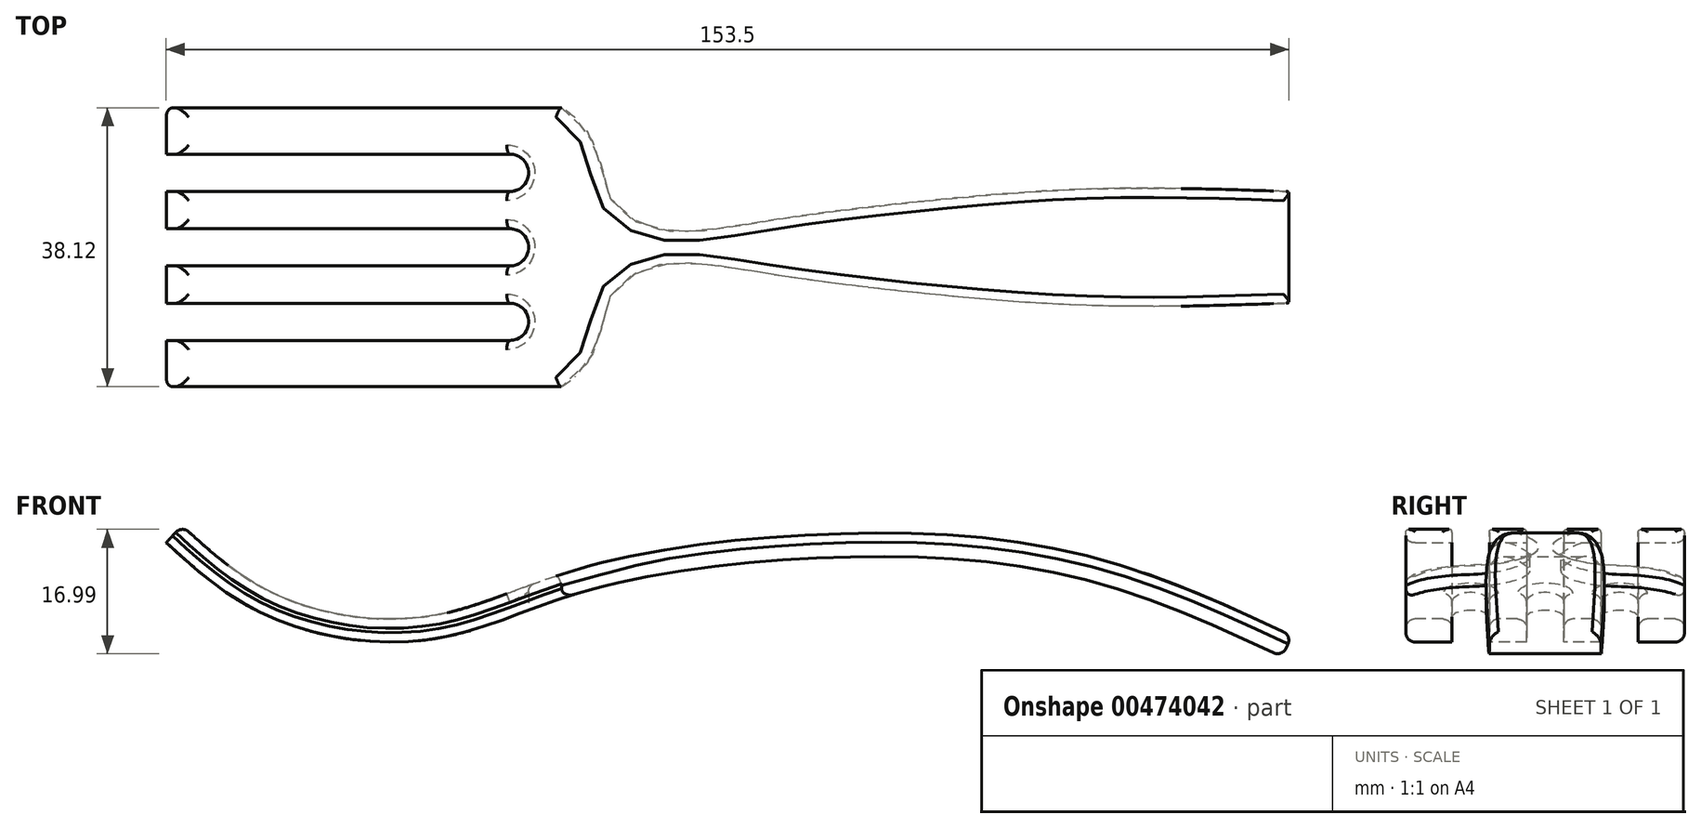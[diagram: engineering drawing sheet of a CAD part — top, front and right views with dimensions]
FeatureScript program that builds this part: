
annotation { "Feature Type Name" : "Feature", "Feature Type Description" : "" }
export const myFeature = defineFeature(function(context is Context, id is Id, definition is map)
    precondition{}
    {
        {
            var Q0;
            Q0=qCreatedBy(makeId("Front.planeOp"),FACE);
            var sketch = newSketch(context, id + "F0", { "sketchPlane" : qUnion([Q0])});
            skFitSpline(sketch, "E0", {"points": [v(-76.59, 15.57) * mm, v(-66.27, 7.44) * mm, v(-53.17, 2.68) * mm, v(-37.7, 2.88) * mm, v(-19.04, 9.03) * mm, v(14.89, 13.6) * mm, v(48.02, 10.81) * mm, v(76, 0) * mm], "startDerivative": vector(88.7, -79.86) * mm, "endDerivative": vector(163.37, -75.33) * mm});
            skFitSpline(sketch, "E1.0", {"points": [v(-74.46, 17.93) * mm, v(-73.54, 17.1) * mm, v(-71.71, 15.46) * mm, v(-68.98, 13.16) * mm, v(-66.66, 11.43) * mm, v(-64.75, 10.21) * mm, v(-62.78, 9.1) * mm, v(-60.15, 7.88) * mm, v(-56.8, 6.72) * mm, v(-53.27, 5.87) * mm, v(-49.6, 5.32) * mm, v(-46.48, 5.16) * mm, v(-43.99, 5.22) * mm, v(-42.12, 5.36) * mm, v(-40.57, 5.56) * mm, v(-39.34, 5.77) * mm, v(-38.42, 5.96) * mm, v(-37.5, 6.18) * mm, v(-36.27, 6.5) * mm, v(-34.7, 6.98) * mm, v(-32.75, 7.64) * mm, v(-30.06, 8.61) * mm, v(-27.2, 9.69) * mm, v(-24.1, 10.78) * mm, v(-21.65, 11.58) * mm, v(-19.04, 12.34) * mm, v(-16.31, 13.03) * mm, v(-13.49, 13.66) * mm, v(-9.6, 14.42) * mm, v(-4.52, 15.21) * mm, v(1.77, 15.95) * mm, v(8.17, 16.47) * mm, v(14.56, 16.79) * mm, v(20.86, 16.91) * mm, v(27.06, 16.81) * mm, v(33.15, 16.45) * mm, v(39.14, 15.8) * mm, v(44.03, 14.97) * mm, v(47.88, 14.13) * mm, v(51.68, 13.16) * mm, v(56.32, 11.73) * mm, v(61.74, 9.74) * mm, v(68.79, 6.82) * mm, v(73.93, 4.45) * mm, v(77.33, 2.88) * mm]});
            skLineSegment(sketch, "E2", {"start": v(-76.59, 15.57) * mm, "end": v(-74.46, 17.93) * mm});
            skLineSegment(sketch, "E3", {"start": v(77.33, 2.88) * mm, "end": v(76, 0) * mm});
            skSolve(sketch);
        }
        {
            var Q0;
            Q0=makeQuery(id+"F0.imprint","IMPRINT",FACE,{"disambiguationData":[TD([[makeQuery(id+"F0.imprint","IMPRINT",EDGE,{"derivedFrom":sQuery(id+"F0.wireOp",EDGE,"E0")}),1.0]])]});
            extrude(context, id + "F1", {"entities" : qUnion([Q0]), "endBound" : BoundingType.SYMMETRIC, "depth" : 38.1 * mm});
        }
        {
            var Q0;
            Q0=qCreatedBy(makeId("Top.planeOp"),FACE);
            var sketch = newSketch(context, id + "F2", { "sketchPlane" : qUnion([Q0])});
            skFitSpline(sketch, "E4", {"points": [v(-25.47, -20.37) * mm, v(-20.21, -17.28) * mm, v(-17.27, -11.89) * mm, v(-16.05, -6.98) * mm, v(-9.92, -2.57) * mm, v(5.27, -3.55) * mm, v(28.8, -6.5) * mm, v(49.38, -7.96) * mm, v(66.05, -7.96) * mm, v(80.75, -7.47) * mm], "startDerivative": vector(70.18, 23.45) * mm, "endDerivative": vector(117.67, 4.45) * mm});
            skFitSpline(sketch, "E5", {"points": [v(0, 0) * mm, v(76.34, 0) * mm], "startDerivative": vector(76.34, 0) * mm, "endDerivative": vector(76.34, 0) * mm, "construction": true});
            skFitSpline(sketch, "E6.MirrorCS", {"points": [v(-25.47, 20.37) * mm, v(-20.21, 17.28) * mm, v(-17.27, 11.89) * mm, v(-16.05, 6.98) * mm, v(-9.92, 2.57) * mm, v(5.27, 3.55) * mm, v(28.8, 6.5) * mm, v(49.38, 7.96) * mm, v(66.05, 7.96) * mm, v(80.75, 7.47) * mm], "startDerivative": vector(70.18, -23.45) * mm, "endDerivative": vector(117.67, -4.45) * mm});
            skLineSegment(sketch, "E7", {"start": v(80.75, -7.47) * mm, "end": v(80.75, 7.47) * mm});
            skLineSegment(sketch, "E8", {"start": v(-25.47, -20.37) * mm, "end": v(-80.38, -20.37) * mm});
            skLineSegment(sketch, "E9", {"start": v(-25.47, 20.37) * mm, "end": v(-80.38, 20.37) * mm});
            skLineSegment(sketch, "E10", {"start": v(-80.38, 20.37) * mm, "end": v(-80.38, 12.72) * mm});
            skPoint(sketch, "E11.endSnap0", {"position": v(-80.38, 0) * mm});
            skLineSegment(sketch, "E12", {"start": v(-80.38, -20.37) * mm, "end": v(-80.38, -12.72) * mm});
            skLineSegment(sketch, "E13.0", {"start": v(-80.38, -12.72) * mm, "end": v(-29.58, -12.72) * mm});
            skLineSegment(sketch, "E14.0", {"start": v(-80.38, -7.64) * mm, "end": v(-29.58, -7.64) * mm});
            skLineSegment(sketch, "E15.0", {"start": v(-80.38, -2.54) * mm, "end": v(-29.58, -2.54) * mm});
            skLineSegment(sketch, "E16.0", {"start": v(-80.38, 2.54) * mm, "end": v(-29.58, 2.54) * mm});
            skLineSegment(sketch, "E17.0", {"start": v(-80.38, 12.72) * mm, "end": v(-29.58, 12.72) * mm});
            skLineSegment(sketch, "E18.0", {"start": v(-80.38, 7.64) * mm, "end": v(-29.58, 7.64) * mm});
            skArc(sketch, "E19", {"start": v(-29.58, -12.72) * mm, "mid": v(-27.04, -10.18) * mm, "end": v(-29.58, -7.64) * mm});
            skArc(sketch, "E20", {"start": v(-29.58, -2.54) * mm, "mid": v(-27.04, 0) * mm, "end": v(-29.58, 2.54) * mm});
            skArc(sketch, "E21", {"start": v(-29.58, 7.64) * mm, "mid": v(-27.04, 10.18) * mm, "end": v(-29.58, 12.72) * mm});
            skLineSegment(sketch, "E22.trimOffspring", {"start": v(-80.38, -12.72) * mm, "end": v(-80.38, -20.37) * mm});
            skLineSegment(sketch, "E23.trimOffspring", {"start": v(-80.38, -7.64) * mm, "end": v(-80.38, -2.54) * mm});
            skLineSegment(sketch, "E24.trimOffspring", {"start": v(-80.38, -2.54) * mm, "end": v(-80.38, -7.64) * mm});
            skLineSegment(sketch, "E25.trimOffspring", {"start": v(-80.38, 7.64) * mm, "end": v(-80.38, 2.54) * mm});
            skSolve(sketch);
        }
        {
            var Q0;
            Q0=makeQuery(id+"F2.imprint","IMPRINT",FACE,{"disambiguationData":[TD([[makeQuery(id+"F2.imprint","IMPRINT",EDGE,{"derivedFrom":sQuery(id+"F2.wireOp",EDGE,"E4")}),1.0]])]});
            extrude(context, id + "F3", {"entities" : qUnion([Q0]), "operationType" : NewBodyOperationType.INTERSECT, "depth" : 25.4 * mm});
        }
        {
            var Q0;
            Q0=makeQuery(id+"F3.boolean.opBoolean","INTERSECT",EDGE,{"derivedFrom":[makeQuery(id+"F1.opExtrude","SWEPT_FACE",FACE,{"disambiguationData":[OSD([sQuery(id+"F0.wireOp",EDGE,"E1.0")])]}),makeQuery(id+"F3.boolean.toolComplement.opBoolean","COPY",FACE,{"derivedFrom":makeQuery(id+"F3.opExtrude","SWEPT_FACE",FACE,{"disambiguationData":[OSD([sQuery(id+"F2.wireOp",EDGE,"E4")])]})})]});
            var Q1;
            Q1=makeQuery(id+"F1.opExtrude","CAP_EDGE",EDGE,{"disambiguationData":[OSD([sQuery(id+"F0.wireOp",EDGE,"E1.0")])],"isStart":false});
            var Q2;
            {var subQ0=sQuery(id+"F0.wireOp",EDGE,"E2");var subQ1=sQuery(id+"F0.wireOp",EDGE,"E1.0");Q2=makeQuery(id+"F3.boolean.opBoolean","SPLIT",EDGE,{"disambiguationData":[TD([makeQuery(id+"F3.boolean.toolComplement.opBoolean","COPY",FACE,{"derivedFrom":makeQuery(id+"F3.opExtrude","SWEPT_FACE",FACE,{"disambiguationData":[OSD([sQuery(id+"F2.wireOp",EDGE,"E13.0")])]})})])],"derivedFrom":makeQuery(id+"F1.opExtrude","SWEPT_EDGE",EDGE,{"disambiguationData":[OSD([subQ1,subQ0])]})});}
            var Q3;
            Q3=makeQuery(id+"F3.boolean.opBoolean","INTERSECT",EDGE,{"derivedFrom":[makeQuery(id+"F1.opExtrude","SWEPT_FACE",FACE,{"disambiguationData":[OSD([sQuery(id+"F0.wireOp",EDGE,"E1.0")])]}),makeQuery(id+"F3.boolean.toolComplement.opBoolean","COPY",FACE,{"derivedFrom":makeQuery(id+"F3.opExtrude","SWEPT_FACE",FACE,{"disambiguationData":[OSD([sQuery(id+"F2.wireOp",EDGE,"E13.0")])]})})]});
            var Q4;
            Q4=makeQuery(id+"F3.boolean.opBoolean","INTERSECT",EDGE,{"derivedFrom":[makeQuery(id+"F1.opExtrude","SWEPT_FACE",FACE,{"disambiguationData":[OSD([sQuery(id+"F0.wireOp",EDGE,"E1.0")])]}),makeQuery(id+"F3.boolean.toolComplement.opBoolean","COPY",FACE,{"derivedFrom":makeQuery(id+"F3.opExtrude","SWEPT_FACE",FACE,{"disambiguationData":[OSD([sQuery(id+"F2.wireOp",EDGE,"E19")])]})})]});
            var Q5;
            Q5=makeQuery(id+"F1.opExtrude","SWEPT_FACE",FACE,{"disambiguationData":[OSD([sQuery(id+"F0.wireOp",EDGE,"E1.0")])]});
            var Q6;
            Q6=makeQuery(id+"F3.boolean.opBoolean","INTERSECT",EDGE,{"derivedFrom":[makeQuery(id+"F1.opExtrude","SWEPT_FACE",FACE,{"disambiguationData":[OSD([sQuery(id+"F0.wireOp",EDGE,"E1.0")])]}),makeQuery(id+"F3.boolean.toolComplement.opBoolean","COPY",FACE,{"derivedFrom":makeQuery(id+"F3.opExtrude","SWEPT_FACE",FACE,{"disambiguationData":[OSD([sQuery(id+"F2.wireOp",EDGE,"E15.0")])]})})]});
            var Q7;
            Q7=makeQuery(id+"F3.boolean.opBoolean","INTERSECT",EDGE,{"derivedFrom":[makeQuery(id+"F1.opExtrude","SWEPT_FACE",FACE,{"disambiguationData":[OSD([sQuery(id+"F0.wireOp",EDGE,"E1.0")])]}),makeQuery(id+"F3.boolean.toolComplement.opBoolean","COPY",FACE,{"derivedFrom":makeQuery(id+"F3.opExtrude","SWEPT_FACE",FACE,{"disambiguationData":[OSD([sQuery(id+"F2.wireOp",EDGE,"E20")])]})})]});
            fillet(context, id + "F4", {"entities" : qUnion([Q0, Q1, Q2, Q3, Q4, Q5, Q6, Q7]), "radius" : 1.27 * mm, "tangentPropagation" : true, "allowEdgeOverflow" : false});
        }
        {
            var Q0;
            Q0=makeQuery(id+"F1.opExtrude","CAP_EDGE",EDGE,{"disambiguationData":[OSD([sQuery(id+"F0.wireOp",EDGE,"E0")])],"isStart":false});
            var Q1;
            Q1=makeQuery(id+"F3.boolean.opBoolean","INTERSECT",EDGE,{"derivedFrom":[makeQuery(id+"F1.opExtrude","SWEPT_FACE",FACE,{"disambiguationData":[OSD([sQuery(id+"F0.wireOp",EDGE,"E0")])]}),makeQuery(id+"F3.boolean.toolComplement.opBoolean","COPY",FACE,{"derivedFrom":makeQuery(id+"F3.opExtrude","SWEPT_FACE",FACE,{"disambiguationData":[OSD([sQuery(id+"F2.wireOp",EDGE,"E4")])]})})]});
            var Q2;
            Q2=makeQuery(id+"F3.boolean.opBoolean","INTERSECT",EDGE,{"derivedFrom":[makeQuery(id+"F1.opExtrude","SWEPT_FACE",FACE,{"disambiguationData":[OSD([sQuery(id+"F0.wireOp",EDGE,"E0")])]}),makeQuery(id+"F3.boolean.toolComplement.opBoolean","COPY",FACE,{"derivedFrom":makeQuery(id+"F3.opExtrude","SWEPT_FACE",FACE,{"disambiguationData":[OSD([sQuery(id+"F2.wireOp",EDGE,"E6.MirrorCS")])]})})]});
            var Q3;
            Q3=makeQuery(id+"F1.opExtrude","CAP_EDGE",EDGE,{"disambiguationData":[OSD([sQuery(id+"F0.wireOp",EDGE,"E0")])],"isStart":true});
            var Q4;
            Q4=makeQuery(id+"F3.boolean.opBoolean","INTERSECT",EDGE,{"derivedFrom":[makeQuery(id+"F1.opExtrude","SWEPT_FACE",FACE,{"disambiguationData":[OSD([sQuery(id+"F0.wireOp",EDGE,"E0")])]}),makeQuery(id+"F3.boolean.toolComplement.opBoolean","COPY",FACE,{"derivedFrom":makeQuery(id+"F3.opExtrude","SWEPT_FACE",FACE,{"disambiguationData":[OSD([sQuery(id+"F2.wireOp",EDGE,"E17.0")])]})})]});
            var Q5;
            Q5=makeQuery(id+"F3.boolean.opBoolean","INTERSECT",EDGE,{"derivedFrom":[makeQuery(id+"F1.opExtrude","SWEPT_FACE",FACE,{"disambiguationData":[OSD([sQuery(id+"F0.wireOp",EDGE,"E0")])]}),makeQuery(id+"F3.boolean.toolComplement.opBoolean","COPY",FACE,{"derivedFrom":makeQuery(id+"F3.opExtrude","SWEPT_FACE",FACE,{"disambiguationData":[OSD([sQuery(id+"F2.wireOp",EDGE,"E18.0")])]})})]});
            var Q6;
            Q6=makeQuery(id+"F3.boolean.opBoolean","INTERSECT",EDGE,{"derivedFrom":[makeQuery(id+"F1.opExtrude","SWEPT_FACE",FACE,{"disambiguationData":[OSD([sQuery(id+"F0.wireOp",EDGE,"E0")])]}),makeQuery(id+"F3.boolean.toolComplement.opBoolean","COPY",FACE,{"derivedFrom":makeQuery(id+"F3.opExtrude","SWEPT_FACE",FACE,{"disambiguationData":[OSD([sQuery(id+"F2.wireOp",EDGE,"E21")])]})})]});
            var Q7;
            Q7=makeQuery(id+"F3.boolean.opBoolean","INTERSECT",EDGE,{"derivedFrom":[makeQuery(id+"F1.opExtrude","SWEPT_FACE",FACE,{"disambiguationData":[OSD([sQuery(id+"F0.wireOp",EDGE,"E0")])]}),makeQuery(id+"F3.boolean.toolComplement.opBoolean","COPY",FACE,{"derivedFrom":makeQuery(id+"F3.opExtrude","SWEPT_FACE",FACE,{"disambiguationData":[OSD([sQuery(id+"F2.wireOp",EDGE,"E16.0")])]})})]});
            var Q8;
            Q8=makeQuery(id+"F3.boolean.opBoolean","INTERSECT",EDGE,{"derivedFrom":[makeQuery(id+"F1.opExtrude","SWEPT_FACE",FACE,{"disambiguationData":[OSD([sQuery(id+"F0.wireOp",EDGE,"E0")])]}),makeQuery(id+"F3.boolean.toolComplement.opBoolean","COPY",FACE,{"derivedFrom":makeQuery(id+"F3.opExtrude","SWEPT_FACE",FACE,{"disambiguationData":[OSD([sQuery(id+"F2.wireOp",EDGE,"E20")])]})})]});
            var Q9;
            Q9=makeQuery(id+"F3.boolean.opBoolean","INTERSECT",EDGE,{"derivedFrom":[makeQuery(id+"F1.opExtrude","SWEPT_FACE",FACE,{"disambiguationData":[OSD([sQuery(id+"F0.wireOp",EDGE,"E0")])]}),makeQuery(id+"F3.boolean.toolComplement.opBoolean","COPY",FACE,{"derivedFrom":makeQuery(id+"F3.opExtrude","SWEPT_FACE",FACE,{"disambiguationData":[OSD([sQuery(id+"F2.wireOp",EDGE,"E15.0")])]})})]});
            var Q10;
            Q10=makeQuery(id+"F3.boolean.opBoolean","INTERSECT",EDGE,{"derivedFrom":[makeQuery(id+"F1.opExtrude","SWEPT_FACE",FACE,{"disambiguationData":[OSD([sQuery(id+"F0.wireOp",EDGE,"E0")])]}),makeQuery(id+"F3.boolean.toolComplement.opBoolean","COPY",FACE,{"derivedFrom":makeQuery(id+"F3.opExtrude","SWEPT_FACE",FACE,{"disambiguationData":[OSD([sQuery(id+"F2.wireOp",EDGE,"E14.0")])]})})]});
            var Q11;
            Q11=makeQuery(id+"F3.boolean.opBoolean","INTERSECT",EDGE,{"derivedFrom":[makeQuery(id+"F1.opExtrude","SWEPT_FACE",FACE,{"disambiguationData":[OSD([sQuery(id+"F0.wireOp",EDGE,"E0")])]}),makeQuery(id+"F3.boolean.toolComplement.opBoolean","COPY",FACE,{"derivedFrom":makeQuery(id+"F3.opExtrude","SWEPT_FACE",FACE,{"disambiguationData":[OSD([sQuery(id+"F2.wireOp",EDGE,"E13.0")])]})})]});
            var Q12;
            {var subQ0=sQuery(id+"F0.wireOp",EDGE,"E0");var subQ1=sQuery(id+"F0.wireOp",EDGE,"E2");Q12=makeQuery(id+"F3.boolean.opBoolean","SPLIT",EDGE,{"disambiguationData":[TD([makeQuery(id+"F3.boolean.toolComplement.opBoolean","COPY",FACE,{"derivedFrom":makeQuery(id+"F3.opExtrude","SWEPT_FACE",FACE,{"disambiguationData":[OSD([sQuery(id+"F2.wireOp",EDGE,"E14.0")])]})})])],"derivedFrom":makeQuery(id+"F1.opExtrude","SWEPT_EDGE",EDGE,{"disambiguationData":[OSD([subQ0,subQ1])]})});}
            var Q13;
            {var subQ0=sQuery(id+"F0.wireOp",EDGE,"E0");var subQ1=sQuery(id+"F0.wireOp",EDGE,"E2");Q13=makeQuery(id+"F3.boolean.opBoolean","SPLIT",EDGE,{"disambiguationData":[TD([makeQuery(id+"F3.boolean.toolComplement.opBoolean","COPY",FACE,{"derivedFrom":makeQuery(id+"F3.opExtrude","SWEPT_FACE",FACE,{"disambiguationData":[OSD([sQuery(id+"F2.wireOp",EDGE,"E13.0")])]})})])],"derivedFrom":makeQuery(id+"F1.opExtrude","SWEPT_EDGE",EDGE,{"disambiguationData":[OSD([subQ0,subQ1])]})});}
            var Q14;
            {var subQ0=sQuery(id+"F0.wireOp",EDGE,"E0");var subQ1=sQuery(id+"F0.wireOp",EDGE,"E2");Q14=makeQuery(id+"F3.boolean.opBoolean","SPLIT",EDGE,{"disambiguationData":[TD([makeQuery(id+"F3.boolean.toolComplement.opBoolean","COPY",FACE,{"derivedFrom":makeQuery(id+"F3.opExtrude","SWEPT_FACE",FACE,{"disambiguationData":[OSD([sQuery(id+"F2.wireOp",EDGE,"E16.0")])]})})])],"derivedFrom":makeQuery(id+"F1.opExtrude","SWEPT_EDGE",EDGE,{"disambiguationData":[OSD([subQ0,subQ1])]})});}
            var Q15;
            {var subQ0=sQuery(id+"F0.wireOp",EDGE,"E0");var subQ1=sQuery(id+"F0.wireOp",EDGE,"E2");Q15=makeQuery(id+"F3.boolean.opBoolean","SPLIT",EDGE,{"disambiguationData":[TD([makeQuery(id+"F3.boolean.toolComplement.opBoolean","COPY",FACE,{"derivedFrom":makeQuery(id+"F3.opExtrude","SWEPT_FACE",FACE,{"disambiguationData":[OSD([sQuery(id+"F2.wireOp",EDGE,"E17.0")])]})})])],"derivedFrom":makeQuery(id+"F1.opExtrude","SWEPT_EDGE",EDGE,{"disambiguationData":[OSD([subQ0,subQ1])]})});}
            var Q16;
            Q16=makeQuery(id+"F1.opExtrude","SWEPT_EDGE",EDGE,{"disambiguationData":[OSD([sQuery(id+"F0.wireOp",EDGE,"E0"),sQuery(id+"F0.wireOp",EDGE,"E3")])]});
            fillet(context, id + "F5", {"entities" : qUnion([Q0, Q1, Q2, Q3, Q4, Q5, Q6, Q7, Q8, Q9, Q10, Q11, Q12, Q13, Q14, Q15, Q16]), "radius" : 1.27 * mm, "tangentPropagation" : true, "allowEdgeOverflow" : false});
        }
    });
